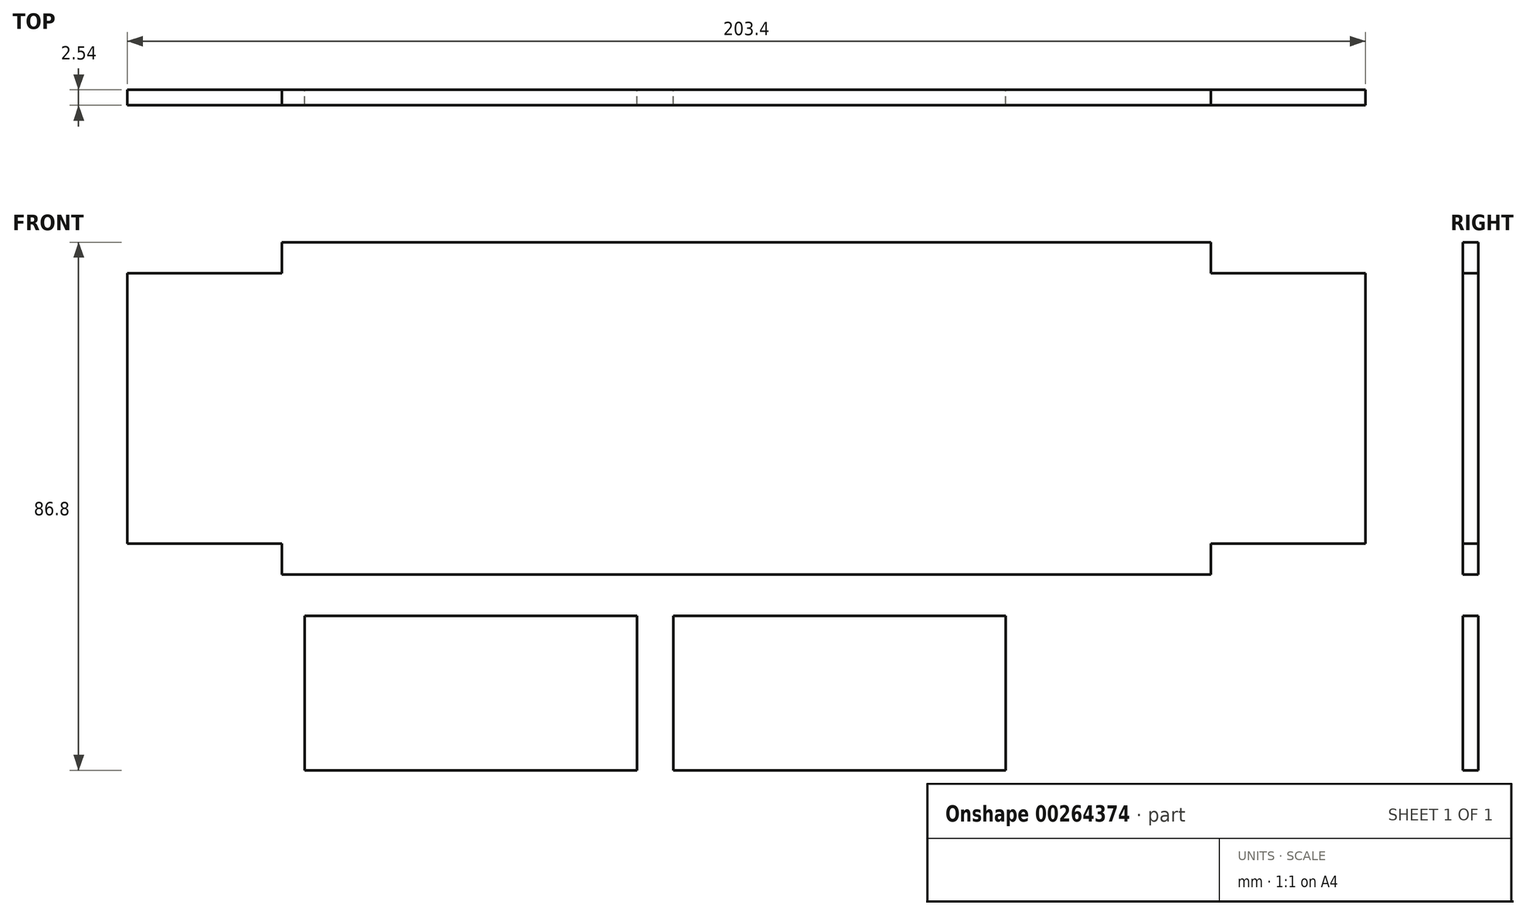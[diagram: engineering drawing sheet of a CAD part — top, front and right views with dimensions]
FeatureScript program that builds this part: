
annotation { "Feature Type Name" : "Feature", "Feature Type Description" : "" }
export const myFeature = defineFeature(function(context is Context, id is Id, definition is map)
    precondition{}
    {
        {
            var Q0;
            Q0=qCreatedBy(makeId("Front.planeOp"),FACE);
            var sketch = newSketch(context, id + "F0", { "sketchPlane" : qUnion([Q0])});
            skLineSegment(sketch, "E0", {"start": v(-52.83, -22.58) * mm, "end": v(99.77, -22.58) * mm});
            skLineSegment(sketch, "E1", {"start": v(-52.83, -22.58) * mm, "end": v(-52.83, -17.5) * mm});
            skLineSegment(sketch, "E2", {"start": v(-52.83, -17.5) * mm, "end": v(-78.23, -17.5) * mm});
            skLineSegment(sketch, "E3", {"start": v(-78.23, -17.5) * mm, "end": v(-78.23, 26.95) * mm});
            skLineSegment(sketch, "E4", {"start": v(-78.23, 26.95) * mm, "end": v(-52.83, 26.95) * mm});
            skLineSegment(sketch, "E5", {"start": v(-52.83, 26.95) * mm, "end": v(-52.83, 32.03) * mm});
            skLineSegment(sketch, "E6", {"start": v(-52.83, 32.03) * mm, "end": v(99.77, 32.03) * mm});
            skLineSegment(sketch, "E7", {"start": v(99.77, 32.03) * mm, "end": v(99.77, 26.95) * mm});
            skLineSegment(sketch, "E8", {"start": v(99.77, 26.95) * mm, "end": v(125.17, 26.95) * mm});
            skLineSegment(sketch, "E9", {"start": v(125.17, 26.95) * mm, "end": v(125.17, -17.5) * mm});
            skLineSegment(sketch, "E10", {"start": v(125.17, -17.5) * mm, "end": v(99.77, -17.5) * mm});
            skLineSegment(sketch, "E11", {"start": v(99.77, -17.5) * mm, "end": v(99.77, -22.58) * mm});
            skLineSegment(sketch, "E12", {"start": v(-49.12, -54.77) * mm, "end": v(-49.12, -29.37) * mm});
            skLineSegment(sketch, "E13", {"start": v(-49.12, -29.37) * mm, "end": v(5.5, -29.37) * mm});
            skLineSegment(sketch, "E14", {"start": v(5.5, -29.37) * mm, "end": v(5.5, -54.77) * mm});
            skLineSegment(sketch, "E15", {"start": v(5.5, -54.77) * mm, "end": v(-49.12, -54.77) * mm});
            skLineSegment(sketch, "E16", {"start": v(11.45, -54.77) * mm, "end": v(11.45, -29.37) * mm});
            skPoint(sketch, "E16.startSnap0", {"position": v(-21.81, -54.77) * mm});
            skLineSegment(sketch, "E17", {"start": v(11.45, -29.37) * mm, "end": v(66.06, -29.37) * mm});
            skLineSegment(sketch, "E18", {"start": v(66.06, -29.37) * mm, "end": v(66.06, -54.77) * mm});
            skLineSegment(sketch, "E19", {"start": v(66.06, -54.77) * mm, "end": v(11.45, -54.77) * mm});
            skSolve(sketch);
        }
        {
            var Q0;
            Q0=makeQuery(id+"F0.imprint","IMPRINT",FACE,{"disambiguationData":[TD([[makeQuery(id+"F0.imprint","IMPRINT",EDGE,{"derivedFrom":sQuery(id+"F0.wireOp",EDGE,"E0")}),1.0]])]});
            var Q1;
            Q1=makeQuery(id+"F0.imprint","IMPRINT",FACE,{"disambiguationData":[TD([[makeQuery(id+"F0.imprint","IMPRINT",EDGE,{"derivedFrom":sQuery(id+"F0.wireOp",EDGE,"E16")}),-1.0]])]});
            var Q2;
            Q2=makeQuery(id+"F0.imprint","IMPRINT",FACE,{"disambiguationData":[TD([[makeQuery(id+"F0.imprint","IMPRINT",EDGE,{"derivedFrom":sQuery(id+"F0.wireOp",EDGE,"E12")}),-1.0]])]});
            extrude(context, id + "F1", {"entities" : qUnion([Q0, Q1, Q2]), "depth" : 2.54 * mm});
        }
    });
